# Revit family: DE_MEAKERB BRIDGE 160-125 und 160-150 Dehnfugen-Set
name_source: partatom
category: Allgemeines Modell
units: mm (PartAtom-declared; Revit-internal decimal feet)

## family parameters
Basisbauteil = Fläche
Beim Laden mit Abzugskörper schneiden = Nein
Bemaßung runder Anschluss = Durchmesser verwenden
Beschriftungsausrichtung beibehalten = Nein
Gemeinsam genutzt = Nein
Kann Basisbauteil für Bewehrung sein = Nein
OmniClass-Nummer = 23.70.50.00
OmniClass-Titel = Liquid Waste Handling Services
Raumberechnungspunkt = Nein
Teiletyp = Normal

## types (1)
- MEAKERB BRIDGE 160.Dehnungsfugen-Set-1.3 m für ungehinderten Wasserfluss über Dehnungsfugen
    Artikelnummer = 010152237
    Ausführungsunterlagen = gemäß Zeichnung und Einzelbeschreibung
    Ausschreiben.de = https://www.ausschreiben.de
    Bauelement = Entwässerungsrinnen Oberflächenwasser
    Baustoff, Bettung/Fundament = -
    Bauteil, Entwässerung = Entwässerungsrinne
    Beschreibung = Universal Entwässerungssystem aus Polymerbeton für Belastungsklassen bis E600
    Breite = 220 mm  [stored 0.721785 ft]
    Einbautechnologie = siehe Einbauanleitung
    Gewicht = 60.5KGM
    Hersteller = MEA Bautechnik GmbH Geschäftsbereich MEA Water Management
    Hersteller und Typ - Ausschreibender gleichwertig = wie MEA Bautechnik GmbH, Modell MEA…...
    Höhe = 200 mm  [stored 0.656168 ft]
    Konstruktion Entwässerungsbauteil = Hohlbordrinne für Brücken
    MEA Planungshilfe = https://www.mea-group.com
    Material = Polymerbeton
    Modell = Bridge 160 Expansion
    Nennweite mm Entwässerungsbauteil = https://www.nennweite-group.com
    Produktwebsite = https://www.mea-group.com
    STLB Bau Mustervorlage = https://www.stlb-bau-online.de
    Technische Produktinformation = https://www.mea-group.com
    Typ Entwässerungsrinne = Typ M
    URL = https://www.mea-group.com
    Vorgabe-Ansicht = 0 mm  [stored 0 ft]
    Werkstoff, Abdeckung = Metall - Edelstahl satiniert
    guid = cf6c1bd8-9bf4-4563-8c57-07955e2378ac

note: [stored X ft] marks values corroborated as IEEE doubles in the binary element streams (Revit-internal decimal feet)
